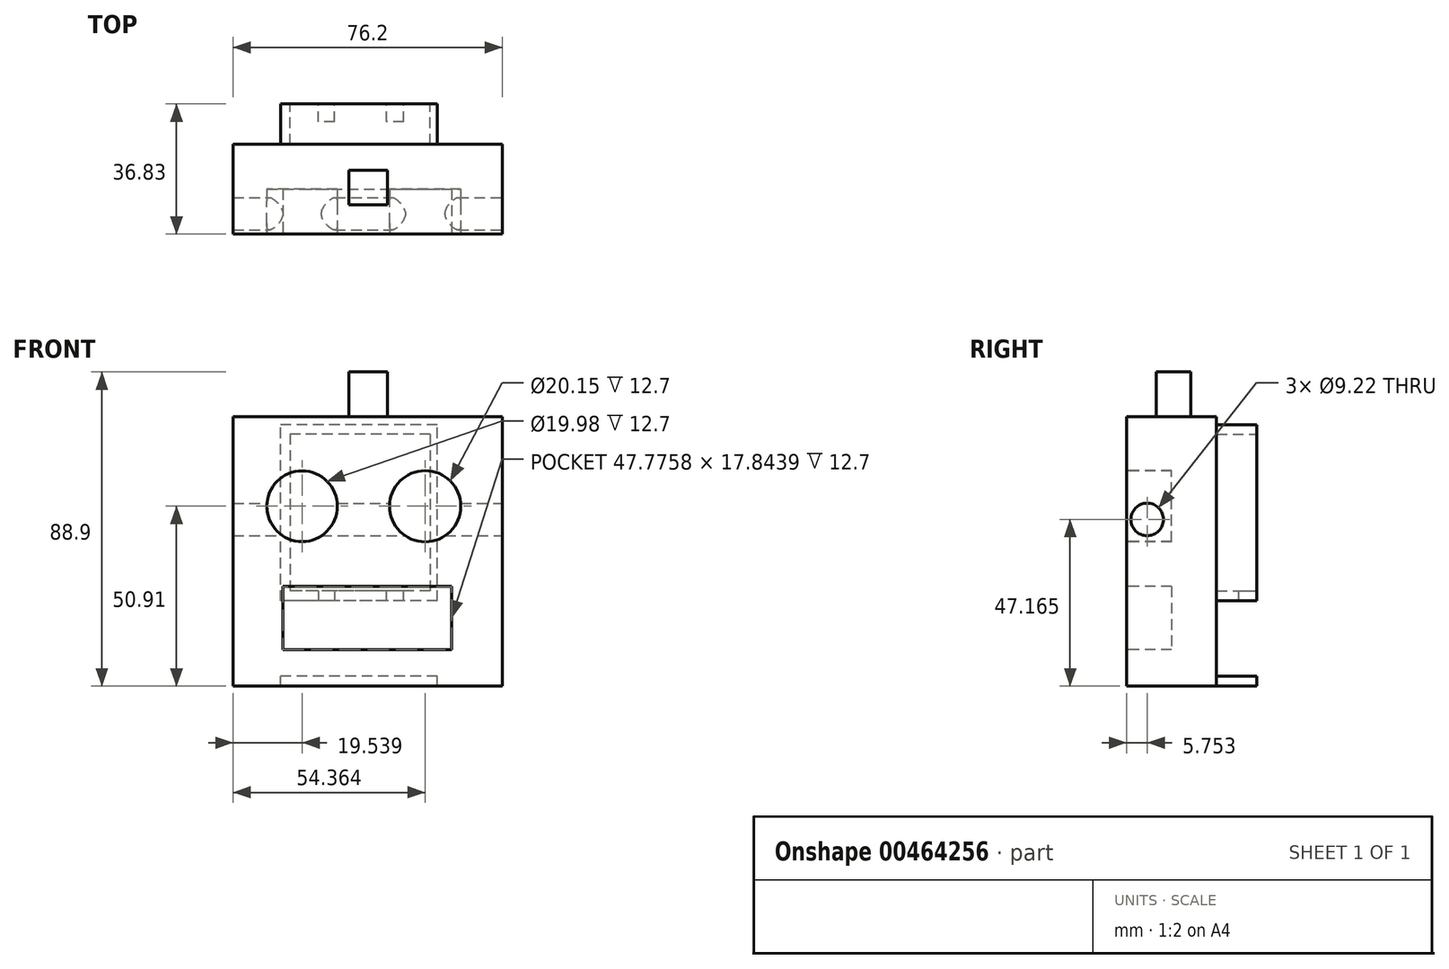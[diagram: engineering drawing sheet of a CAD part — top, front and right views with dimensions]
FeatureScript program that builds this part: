
annotation { "Feature Type Name" : "Feature", "Feature Type Description" : "" }
export const myFeature = defineFeature(function(context is Context, id is Id, definition is map)
    precondition{}
    {
        {
            var Q0;
            Q0=qCreatedBy(makeId("Front.planeOp"),FACE);
            var sketch = newSketch(context, id + "F0", { "sketchPlane" : qUnion([Q0])});
            skLineSegment(sketch, "E0.bottom", {"start": v(-48.32, 39.68) * mm, "end": v(27.88, 39.68) * mm});
            skLineSegment(sketch, "E0.top", {"start": v(-48.32, -36.52) * mm, "end": v(27.88, -36.52) * mm});
            skLineSegment(sketch, "E0.left", {"start": v(-48.32, 39.68) * mm, "end": v(-48.32, -36.52) * mm});
            skLineSegment(sketch, "E0.right", {"start": v(27.88, 39.68) * mm, "end": v(27.88, -36.52) * mm});
            skSolve(sketch);
        }
        {
            var Q0;
            Q0=makeQuery(id+"F0.imprint","IMPRINT",FACE,{"disambiguationData":[TD([[makeQuery(id+"F0.imprint","IMPRINT",EDGE,{"derivedFrom":sQuery(id+"F0.wireOp",EDGE,"E0.bottom")}),-1.0]])]});
            extrude(context, id + "F1", {"entities" : qUnion([Q0]), "oppositeDirection" : true, "depth" : 25.4 * mm});
        }
        {
            var Q0;
            Q0=makeQuery(id+"F1.opExtrude","CAP_FACE",FACE,{"disambiguationData":[OSD([sQuery(id+"F0.wireOp",EDGE,"E0.bottom"),sQuery(id+"F0.wireOp",EDGE,"E0.top"),sQuery(id+"F0.wireOp",EDGE,"E0.left"),sQuery(id+"F0.wireOp",EDGE,"E0.right")])],"isStart":true});
            var sketch = newSketch(context, id + "F2", { "sketchPlane" : qUnion([Q0])});
            skCircle(sketch, "E1", {"center": v(-28.78, 14.4) * mm, "radius": 10 * mm});
            skCircle(sketch, "E2", {"center": v(6.04, 14.4) * mm, "radius": 10.08 * mm});
            skSolve(sketch);
        }
        {
            var Q0;
            Q0=makeQuery(id+"F2.imprint","IMPRINT",FACE,{"disambiguationData":[TD([[makeQuery(id+"F2.imprint","IMPRINT",EDGE,{"derivedFrom":sQuery(id+"F2.wireOp",EDGE,"E1")}),1.0]])]});
            var Q1;
            Q1=makeQuery(id+"F2.imprint","IMPRINT",FACE,{"disambiguationData":[TD([[makeQuery(id+"F2.imprint","IMPRINT",EDGE,{"derivedFrom":sQuery(id+"F2.wireOp",EDGE,"E2")}),1.0]])]});
            extrude(context, id + "F3", {"entities" : qUnion([Q0, Q1]), "operationType" : NewBodyOperationType.REMOVE, "oppositeDirection" : true, "depth" : 12.7 * mm});
        }
        {
            var Q0;
            Q0=makeQuery(id+"F1.opExtrude","CAP_FACE",FACE,{"disambiguationData":[OSD([sQuery(id+"F0.wireOp",EDGE,"E0.bottom"),sQuery(id+"F0.wireOp",EDGE,"E0.top"),sQuery(id+"F0.wireOp",EDGE,"E0.left"),sQuery(id+"F0.wireOp",EDGE,"E0.right")])],"isStart":true});
            var sketch = newSketch(context, id + "F4", { "sketchPlane" : qUnion([Q0])});
            skLineSegment(sketch, "E3.bottom", {"start": v(-34.25, -8.35) * mm, "end": v(13.53, -8.35) * mm});
            skLineSegment(sketch, "E3.top", {"start": v(-34.25, -26.2) * mm, "end": v(13.53, -26.2) * mm});
            skLineSegment(sketch, "E3.left", {"start": v(-34.25, -8.35) * mm, "end": v(-34.25, -26.2) * mm});
            skLineSegment(sketch, "E3.right", {"start": v(13.53, -8.35) * mm, "end": v(13.53, -26.2) * mm});
            skSolve(sketch);
        }
        {
            var Q0;
            Q0=makeQuery(id+"F4.imprint","IMPRINT",FACE,{"disambiguationData":[TD([[makeQuery(id+"F4.imprint","IMPRINT",EDGE,{"derivedFrom":sQuery(id+"F4.wireOp",EDGE,"E3.bottom")}),-1.0]])]});
            extrude(context, id + "F5", {"entities" : qUnion([Q0]), "operationType" : NewBodyOperationType.REMOVE, "oppositeDirection" : true, "depth" : 12.7 * mm});
        }
        {
            var Q0;
            Q0=makeQuery(id+"F1.opExtrude","SWEPT_FACE",FACE,{"disambiguationData":[OSD([sQuery(id+"F0.wireOp",EDGE,"E0.right")])]});
            var sketch = newSketch(context, id + "F6", { "sketchPlane" : qUnion([Q0])});
            skCircle(sketch, "E4", {"center": v(5.75, 10.64) * mm, "radius": 4.61 * mm});
            skSolve(sketch);
        }
        {
            var Q0;
            Q0=makeQuery(id+"F6.imprint","IMPRINT",FACE,{"disambiguationData":[TD([[makeQuery(id+"F6.imprint","IMPRINT",EDGE,{"derivedFrom":sQuery(id+"F6.wireOp",EDGE,"E4")}),1.0]])]});
            extrude(context, id + "F7", {"entities" : qUnion([Q0]), "operationType" : NewBodyOperationType.REMOVE, "oppositeDirection" : true, "depth" : 127 * mm});
        }
        {
            var Q0;
            Q0=makeQuery(id+"F1.opExtrude","CAP_FACE",FACE,{"disambiguationData":[OSD([sQuery(id+"F0.wireOp",EDGE,"E0.bottom"),sQuery(id+"F0.wireOp",EDGE,"E0.top"),sQuery(id+"F0.wireOp",EDGE,"E0.left"),sQuery(id+"F0.wireOp",EDGE,"E0.right")])],"isStart":false});
            var sketch = newSketch(context, id + "F8", { "sketchPlane" : qUnion([Q0])});
            skLineSegment(sketch, "E5.bottom", {"start": v(-9.5, -12.38) * mm, "end": v(34.82, -12.38) * mm});
            skLineSegment(sketch, "E5.top", {"start": v(-9.5, 37.41) * mm, "end": v(34.82, 37.41) * mm});
            skLineSegment(sketch, "E5.left", {"start": v(-9.5, -12.38) * mm, "end": v(-9.5, 37.41) * mm});
            skLineSegment(sketch, "E5.right", {"start": v(34.82, -12.38) * mm, "end": v(34.82, 37.41) * mm});
            skSolve(sketch);
        }
        {
            var Q0;
            Q0=makeQuery(id+"F8.imprint","IMPRINT",FACE,{"disambiguationData":[TD([[makeQuery(id+"F8.imprint","IMPRINT",EDGE,{"derivedFrom":sQuery(id+"F8.wireOp",EDGE,"E5.bottom")}),1.0]])]});
            extrude(context, id + "F9", {"entities" : qUnion([Q0]), "operationType" : NewBodyOperationType.ADD, "depth" : 11.43 * mm});
        }
        {
            var Q0;
            Q0=makeQuery(id+"F9.opExtrude","CAP_FACE",FACE,{"disambiguationData":[OSD([sQuery(id+"F8.wireOp",EDGE,"E5.bottom"),sQuery(id+"F8.wireOp",EDGE,"E5.top"),sQuery(id+"F8.wireOp",EDGE,"E5.left"),sQuery(id+"F8.wireOp",EDGE,"E5.right")])],"isStart":false});
            var sketch = newSketch(context, id + "F10", { "sketchPlane" : qUnion([Q0])});
            skLineSegment(sketch, "E6.bottom", {"start": v(-7.48, 34.82) * mm, "end": v(32.23, 34.82) * mm});
            skLineSegment(sketch, "E6.top", {"start": v(-7.48, -9.5) * mm, "end": v(32.23, -9.5) * mm});
            skLineSegment(sketch, "E6.left", {"start": v(-7.48, 34.82) * mm, "end": v(-7.48, -9.5) * mm});
            skLineSegment(sketch, "E6.right", {"start": v(32.23, 34.82) * mm, "end": v(32.23, -9.5) * mm});
            skSolve(sketch);
        }
        {
            var Q0;
            Q0=makeQuery(id+"F10.imprint","IMPRINT",FACE,{"disambiguationData":[TD([[makeQuery(id+"F10.imprint","IMPRINT",EDGE,{"derivedFrom":sQuery(id+"F10.wireOp",EDGE,"E6.bottom")}),-1.0]])]});
            extrude(context, id + "F11", {"entities" : qUnion([Q0]), "operationType" : NewBodyOperationType.REMOVE, "oppositeDirection" : true, "depth" : 11.43 * mm});
        }
        {
            var Q0;
            Q0=makeQuery(id+"F1.opExtrude","CAP_FACE",FACE,{"disambiguationData":[OSD([sQuery(id+"F0.wireOp",EDGE,"E0.bottom"),sQuery(id+"F0.wireOp",EDGE,"E0.top"),sQuery(id+"F0.wireOp",EDGE,"E0.left"),sQuery(id+"F0.wireOp",EDGE,"E0.right")])],"isStart":false});
            var sketch = newSketch(context, id + "F12", { "sketchPlane" : qUnion([Q0])});
            skLineSegment(sketch, "E7.bottom", {"start": v(-9.5, -36.52) * mm, "end": v(34.82, -36.52) * mm});
            skLineSegment(sketch, "E7.top", {"start": v(-9.5, -33.67) * mm, "end": v(34.82, -33.67) * mm});
            skLineSegment(sketch, "E7.left", {"start": v(-9.5, -36.52) * mm, "end": v(-9.5, -33.67) * mm});
            skLineSegment(sketch, "E7.right", {"start": v(34.82, -36.52) * mm, "end": v(34.82, -33.67) * mm});
            skSolve(sketch);
        }
        {
            var Q0;
            Q0=makeQuery(id+"F12.imprint","IMPRINT",FACE,{"disambiguationData":[TD([[makeQuery(id+"F12.imprint","IMPRINT",EDGE,{"derivedFrom":sQuery(id+"F12.wireOp",EDGE,"E7.bottom")}),-1.0]])]});
            extrude(context, id + "F13", {"entities" : qUnion([Q0]), "operationType" : NewBodyOperationType.ADD, "depth" : 11.43 * mm});
        }
        {
            var Q0;
            Q0=makeQuery(id+"F9.opExtrude","CAP_FACE",FACE,{"disambiguationData":[OSD([sQuery(id+"F8.wireOp",EDGE,"E5.bottom"),sQuery(id+"F8.wireOp",EDGE,"E5.top"),sQuery(id+"F8.wireOp",EDGE,"E5.left"),sQuery(id+"F8.wireOp",EDGE,"E5.right")])],"isStart":false});
            var sketch = newSketch(context, id + "F14", { "sketchPlane" : qUnion([Q0])});
            skLineSegment(sketch, "E8.bottom", {"start": v(0, -12.38) * mm, "end": v(4.9, -12.38) * mm});
            skLineSegment(sketch, "E8.top", {"start": v(0, -9.5) * mm, "end": v(4.9, -9.5) * mm});
            skLineSegment(sketch, "E8.left", {"start": v(0, -12.38) * mm, "end": v(0, -9.5) * mm});
            skLineSegment(sketch, "E8.right", {"start": v(4.9, -12.38) * mm, "end": v(4.9, -9.5) * mm});
            skLineSegment(sketch, "E9.bottom", {"start": v(19.57, -9.5) * mm, "end": v(24.18, -9.5) * mm});
            skLineSegment(sketch, "E9.top", {"start": v(19.57, -12.38) * mm, "end": v(24.18, -12.38) * mm});
            skLineSegment(sketch, "E9.left", {"start": v(19.57, -9.5) * mm, "end": v(19.57, -12.38) * mm});
            skLineSegment(sketch, "E9.right", {"start": v(24.18, -9.5) * mm, "end": v(24.18, -12.38) * mm});
            skSolve(sketch);
        }
        {
            var Q0;
            Q0=makeQuery(id+"F14.imprint","IMPRINT",FACE,{"disambiguationData":[TD([[makeQuery(id+"F14.imprint","IMPRINT",EDGE,{"derivedFrom":sQuery(id+"F14.wireOp",EDGE,"E9.bottom")}),-1.0]])]});
            var Q1;
            Q1=makeQuery(id+"F14.imprint","IMPRINT",FACE,{"disambiguationData":[TD([[makeQuery(id+"F14.imprint","IMPRINT",EDGE,{"derivedFrom":sQuery(id+"F14.wireOp",EDGE,"E8.bottom")}),1.0]])]});
            extrude(context, id + "F15", {"entities" : qUnion([Q0, Q1]), "operationType" : NewBodyOperationType.REMOVE, "oppositeDirection" : true, "depth" : 5.08 * mm});
        }
        {
            var Q0;
            Q0=makeQuery(id+"F1.opExtrude","SWEPT_FACE",FACE,{"disambiguationData":[OSD([sQuery(id+"F0.wireOp",EDGE,"E0.bottom")])]});
            var sketch = newSketch(context, id + "F16", { "sketchPlane" : qUnion([Q0])});
            skLineSegment(sketch, "E10.bottom", {"start": v(-15.54, 18.11) * mm, "end": v(-4.6, 18.11) * mm});
            skLineSegment(sketch, "E10.top", {"start": v(-15.54, 8.35) * mm, "end": v(-4.6, 8.35) * mm});
            skLineSegment(sketch, "E10.left", {"start": v(-15.54, 18.11) * mm, "end": v(-15.54, 8.35) * mm});
            skLineSegment(sketch, "E10.right", {"start": v(-4.6, 18.11) * mm, "end": v(-4.6, 8.35) * mm});
            skSolve(sketch);
        }
        {
            var Q0;
            Q0=makeQuery(id+"F16.imprint","IMPRINT",FACE,{"disambiguationData":[TD([[makeQuery(id+"F16.imprint","IMPRINT",EDGE,{"derivedFrom":sQuery(id+"F16.wireOp",EDGE,"E10.bottom")}),-1.0]])]});
            extrude(context, id + "F17", {"entities" : qUnion([Q0]), "operationType" : NewBodyOperationType.ADD, "depth" : 12.7 * mm});
        }
    });
